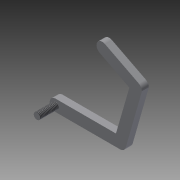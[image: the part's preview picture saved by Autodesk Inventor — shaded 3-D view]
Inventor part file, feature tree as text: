
AUTODESK INVENTOR PART (.ipt)
format: ipt  version: 2015 SP2 (Build 190223200, 223)  size: 94,208 bytes
history: native  units: mm
features: extrude x2, sketch x2, thread x1
ambient origin geometry x8: Origin, YZ Plane, XZ Plane, XY Plane, X Axis, Y Axis, Z Axis, Center Point
bodies: Solid1 (feature_tree)
feature tree (5):
  extrude  "Extrusion1"  Depth=5.0mm
  extrude  "Extrusion2"  Depth=10.0mm
  thread  "Thread3"  [1 undecoded]
  sketch  "Sketch1"  dims[d0=5.0mm d1=5.0mm]
  sketch  "Sketch2"  dims[d2=5.0mm d3=5.0mm d4=3.0mm d5=0.0mm d6=2.8mm d7=8.0mm d8=0.0mm d13=10.0mm d14=0.0mm]
note: 1 required parameter value undecoded (feature->parameter linkage not recoverable at this tier; creation-order binding heuristic only, values carry confidence <= 0.55)
